# Revit family: 306_959ad0af9a0849c68dc43c4c1753ec
name_source: partatom
category: Pipe Accessories
units: mm (PartAtom-declared; Revit-internal decimal feet)

## family parameters
Always vertical = Yes
Cut with Voids When Loaded = No
Part Type = Valve - Breaks Into
Round Connector Dimension = Use Diameter
Shared = No
Work Plane-Based = No

## types (5) — shared parameters
Description = Chrome-pl.thermostatic mixer, setting range 25÷65°C, M conn.
HH = 15 mm  [stored 0.0492126 ft]
HH2 = 8 mm  [stored 0.0262467 ft]
L22 = 2 mm  [stored 0.00656168 ft]
L22__ve = -2 mm  [stored -0.00656168 ft]
L2D = 117 mm
L2D_Min = 3048 mm
L5 = 5 mm  [stored 0.0164042 ft]
LL = 3 mm  [stored 0.00984252 ft]
LL__ve = -3 mm
Manufacturer = FAR
QmdConnectorList = 301;D;302;D
SW = No
W2D = 25 mm  [stored 0.082021 ft]
magiPartTypeId = 306
magiProductFamilyId = 959ad0af9a0849c68dc43c4c1753ec

## per-type parameters (varying)
| type | BC | BC__ve | BNTL | C | CenSd_R2_6 | CenSd_R3_6 | D | H2 | H2HH | H2HH__ve | L2 | LH | LNT | LNT__ve | NT | NT__ve | R1 | R11 | R2 | R21 | R3 | TLL | TLL__ve | magiProductId |
| 3956 1 | 16 mm  [stored 0.0524934 ft] | -16 mm  [stored -0.0524934 ft] | 53 mm | 62 mm | 13 mm | 16 mm  [stored 0.0524934 ft] | 25 mm | 35 mm | 28 mm | -28 mm | 59 mm | 23 mm  [stored 0.0754593 ft] | 49 mm | -49 mm | 15 mm  [stored 0.0492126 ft] | -15 mm  [stored -0.0492126 ft] | 17 mm | 18 mm | 15 mm  [stored 0.0492126 ft] | 16 mm  [stored 0.0524934 ft] | 19 mm | 16 mm  [stored 0.0524934 ft] | -16 mm  [stored -0.0524934 ft] | cc1b9a8ffda54f8f9b0f9ad3b08a21 |
| 3956 112 | 18 mm | -18 mm | 85 mm | 99 mm | 19 mm | 23 mm  [stored 0.0754593 ft] | 40 mm | 34 mm | 26 mm | -26 mm | 85 mm | 22 mm | 75 mm | -75 mm | 21 mm  [stored 0.0688976 ft] | -21 mm | 24 mm  [stored 0.0787402 ft] | 25 mm  [stored 0.082021 ft] | 23 mm  [stored 0.0754593 ft] | 24 mm  [stored 0.0787402 ft] | 26 mm | 15 mm  [stored 0.0492126 ft] | -15 mm  [stored -0.0492126 ft] | b9da9f21669243ce8e16d153099db5 |
| 3956 114 | 18 mm | -18 mm | 81 mm | 94 mm | 16 mm  [stored 0.0524934 ft] | 19 mm | 32 mm | 34 mm | 27 mm | -27 mm | 81 mm | 22 mm | 71 mm | -71 mm | 20 mm  [stored 0.0656168 ft] | -20 mm | 20 mm  [stored 0.0656168 ft] | 21 mm  [stored 0.0688976 ft] | 19 mm | 20 mm  [stored 0.0656168 ft] | 22 mm | 15 mm  [stored 0.0492126 ft] | -15 mm  [stored -0.0492126 ft] | c63f7de5308a424ea08a35c36b2568 |
| 3956 12 | 13 mm | -13 mm | 46 mm | 56 mm | 9 mm  [stored 0.0295276 ft] | 12 mm  [stored 0.0393701 ft] | 15 mm | 35 mm | 28 mm | -28 mm | 51 mm | 23 mm  [stored 0.0754593 ft] | 41 mm | -41 mm | 13 mm | -13 mm | 12 mm  [stored 0.0393701 ft] | 13 mm | 10 mm  [stored 0.0328084 ft] | 11 mm  [stored 0.0360892 ft] | 14 mm  [stored 0.0459318 ft] | 13 mm | -13 mm | 2357c4c71cdb40308c3f05ddf78c0f |
| 3956 34 | 12 mm  [stored 0.0393701 ft] | -12 mm  [stored -0.0393701 ft] | 48 mm | 60 mm | 11 mm  [stored 0.0360892 ft] | 14 mm  [stored 0.0459318 ft] | 20 mm | 35 mm | 28 mm | -28 mm | 56 mm | 23 mm  [stored 0.0754593 ft] | 46 mm | -46 mm  [stored -0.150919 ft] | 14 mm  [stored 0.0459318 ft] | -14 mm  [stored -0.0459318 ft] | 14 mm  [stored 0.0459318 ft] | 15 mm  [stored 0.0492126 ft] | 13 mm | 14 mm  [stored 0.0459318 ft] | 16 mm  [stored 0.0524934 ft] | 12 mm  [stored 0.0393701 ft] | -12 mm  [stored -0.0393701 ft] | 331cf449c5f64ca9af55a8fb4b0ade |

note: column(s) folded — value = type name in every type: MC Product Code

note: [stored X ft] marks values corroborated as IEEE doubles in the binary element streams (Revit-internal decimal feet)

## geometry (parser evidence)
native form markers: Sweep x3
no freeform markers — native parametric forms only
